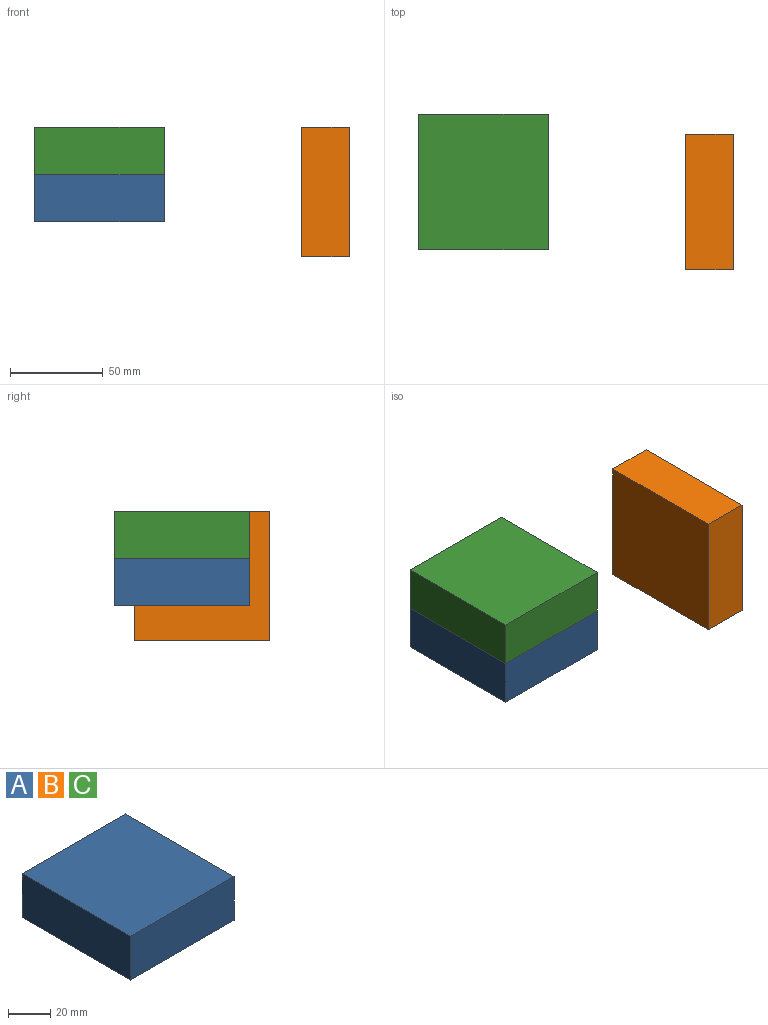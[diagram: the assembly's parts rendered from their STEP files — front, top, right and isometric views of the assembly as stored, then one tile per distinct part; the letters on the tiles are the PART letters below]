
ASSEMBLY  parts=3 mates=2
PART A: 6 faces, bbox 69.4x72.9x25.4 mm
  f0: plane 69.43x25.4mm, normal (0,-1,0), area 1763.6mm2, adj f1,f3,f4,f5
  f1: plane 72.85x25.4mm, normal (1,0,0), area 1850.4mm2, adj f0,f2,f4,f5
  f2: plane 69.43x25.4mm, normal (0,1,0), area 1763.6mm2, adj f1,f3,f4,f5
  f3: plane 72.85x25.4mm, normal (-1,0,0), area 1850.4mm2, adj f0,f2,f4,f5
  f4: plane 72.85x69.43mm, normal (0,0,1), area 5058.2mm2, adj f0,f1,f2,f3
  f5: plane 72.85x69.43mm, normal (0,0,-1), area 5058.2mm2, adj f0,f1,f2,f3
PART B: same geometry as A
PART C: same geometry as A
PLACE A t=(-55.95,-0.91,138.21)mm
PLACE B rot(axis=(0.71,0,0.71),180deg) t=(52.86,-11.58,154.3)mm
PLACE C t=(-55.95,-0.91,163.61)mm
MATE planar B.f1 <-> C.f4  axis (0,0,1) through (65.56,-11.58,189.01)mm
MATE fastened C.f5 <-> A.f4  axis (0,0,-1) through (-55.95,-0.91,163.61)mm
